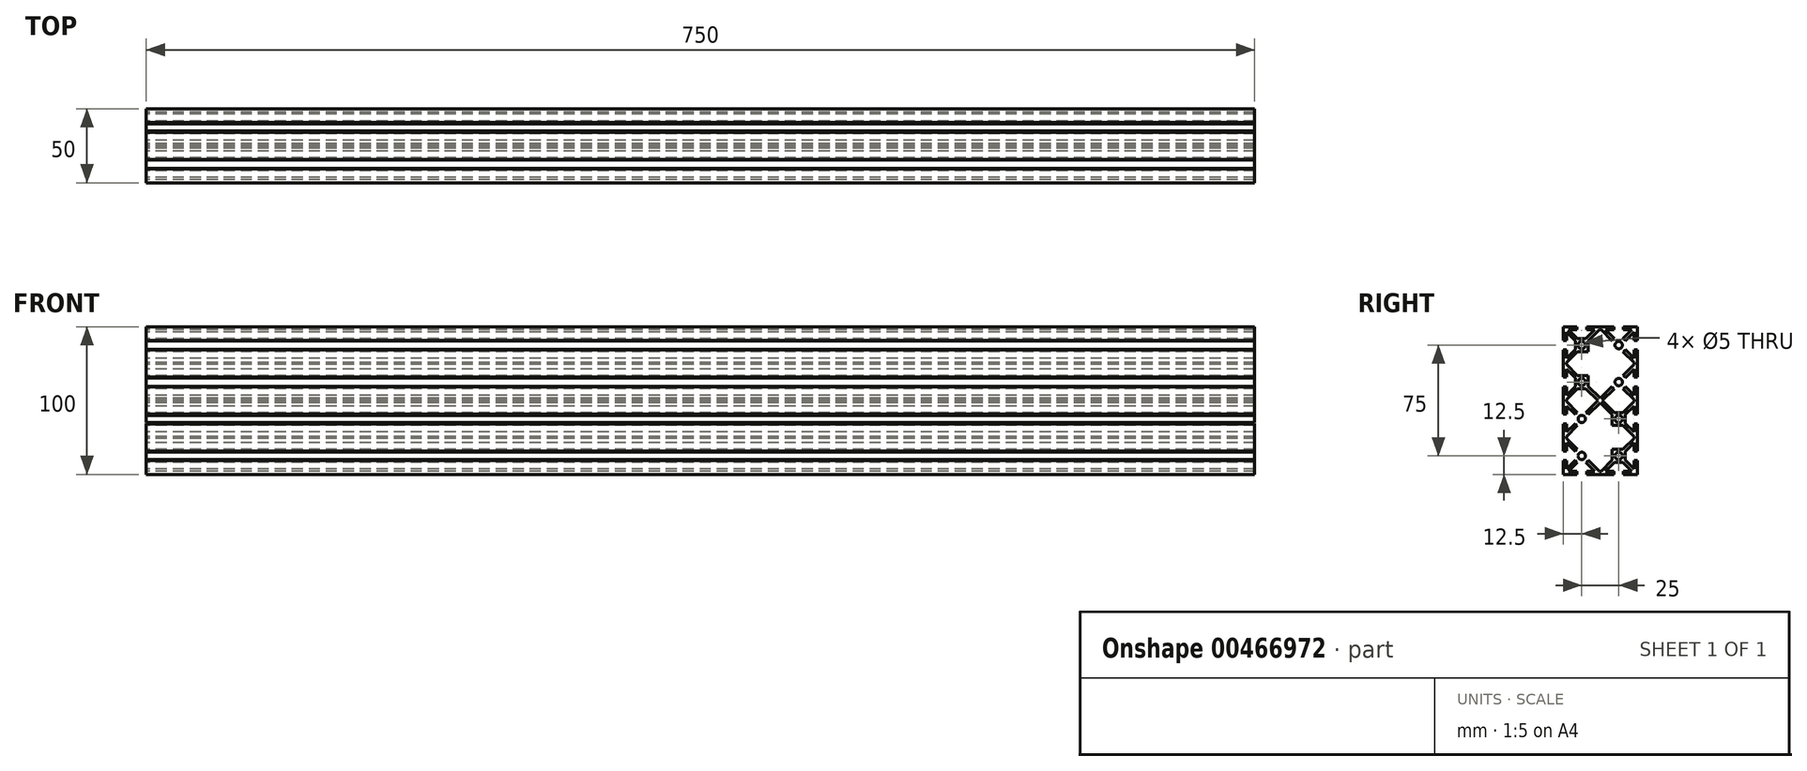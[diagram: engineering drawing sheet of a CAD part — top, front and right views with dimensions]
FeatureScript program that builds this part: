
annotation { "Feature Type Name" : "Feature", "Feature Type Description" : "" }
export const myFeature = defineFeature(function(context is Context, id is Id, definition is map)
    precondition{}
    {
        {
            var Q0;
            Q0=qCreatedBy(makeId("Right.planeOp"),FACE);
            var sketch = newSketch(context, id + "F0", { "sketchPlane" : qUnion([Q0])});
            skLineSegment(sketch, "E0", {"start": v(0, 0) * mm, "end": v(-22.87, 0) * mm, "construction": true});
            skLineSegment(sketch, "E1", {"start": v(0, 0) * mm, "end": v(0, 47.87) * mm, "construction": true});
            skCircle(sketch, "E2", {"center": v(-12.5, 37.5) * mm, "radius": 2.5 * mm});
            skCircle(sketch, "E3", {"center": v(-12.5, 12.5) * mm, "radius": 2.5 * mm});
            skLineSegment(sketch, "E4.bottom", {"start": v(-8.12, 41.88) * mm, "end": v(-16.88, 41.88) * mm});
            skLineSegment(sketch, "E4.top", {"start": v(-8.12, 33.12) * mm, "end": v(-16.88, 33.12) * mm});
            skLineSegment(sketch, "E4.left", {"start": v(-8.12, 41.88) * mm, "end": v(-8.12, 33.12) * mm});
            skLineSegment(sketch, "E4.right", {"start": v(-16.88, 41.88) * mm, "end": v(-16.88, 33.12) * mm});
            skLineSegment(sketch, "E5.bottom", {"start": v(-8.12, 16.88) * mm, "end": v(-16.88, 16.88) * mm});
            skLineSegment(sketch, "E5.top", {"start": v(-8.12, 8.12) * mm, "end": v(-16.88, 8.12) * mm});
            skLineSegment(sketch, "E5.left", {"start": v(-8.12, 16.88) * mm, "end": v(-8.12, 8.12) * mm});
            skLineSegment(sketch, "E5.right", {"start": v(-16.88, 16.88) * mm, "end": v(-16.88, 8.12) * mm});
            skLineSegment(sketch, "E6", {"start": v(0, 50) * mm, "end": v(-9.25, 50) * mm});
            skLineSegment(sketch, "E7", {"start": v(-9.25, 50) * mm, "end": v(-9.25, 47.87) * mm});
            skLineSegment(sketch, "E8", {"start": v(-9.25, 47.87) * mm, "end": v(-3.64, 47.87) * mm});
            skLineSegment(sketch, "E9", {"start": v(-3.64, 47.87) * mm, "end": v(-9.63, 41.88) * mm});
            skLineSegment(sketch, "E10", {"start": v(-15.37, 41.88) * mm, "end": v(-21.36, 47.87) * mm});
            skLineSegment(sketch, "E11", {"start": v(-21.36, 47.87) * mm, "end": v(-15.75, 47.87) * mm});
            skLineSegment(sketch, "E12", {"start": v(-15.75, 47.87) * mm, "end": v(-15.75, 50) * mm});
            skLineSegment(sketch, "E13", {"start": v(-15.75, 50) * mm, "end": v(-25, 50) * mm});
            skLineSegment(sketch, "E14", {"start": v(-25, 50) * mm, "end": v(-25, 40.75) * mm});
            skLineSegment(sketch, "E15", {"start": v(-25, 40.75) * mm, "end": v(-22.87, 40.75) * mm});
            skLineSegment(sketch, "E16", {"start": v(-22.87, 40.75) * mm, "end": v(-22.87, 46.36) * mm});
            skLineSegment(sketch, "E17", {"start": v(-22.87, 46.36) * mm, "end": v(-16.88, 40.37) * mm});
            skLineSegment(sketch, "E18", {"start": v(-16.88, 34.63) * mm, "end": v(-22.87, 28.64) * mm});
            skLineSegment(sketch, "E19", {"start": v(-22.87, 28.64) * mm, "end": v(-22.87, 34.25) * mm});
            skLineSegment(sketch, "E20", {"start": v(-22.87, 34.25) * mm, "end": v(-25, 34.25) * mm});
            skLineSegment(sketch, "E21", {"start": v(-25, 34.25) * mm, "end": v(-25, 15.75) * mm});
            skLineSegment(sketch, "E22", {"start": v(-25, 15.75) * mm, "end": v(-22.87, 15.75) * mm});
            skLineSegment(sketch, "E23", {"start": v(-22.87, 15.75) * mm, "end": v(-22.87, 21.36) * mm});
            skLineSegment(sketch, "E24", {"start": v(-22.87, 21.36) * mm, "end": v(-16.88, 15.37) * mm});
            skLineSegment(sketch, "E25", {"start": v(-16.88, 9.63) * mm, "end": v(-22.87, 3.64) * mm});
            skLineSegment(sketch, "E26", {"start": v(-22.87, 3.64) * mm, "end": v(-22.87, 9.25) * mm});
            skLineSegment(sketch, "E27", {"start": v(-22.87, 9.25) * mm, "end": v(-25, 9.25) * mm});
            skLineSegment(sketch, "E28", {"start": v(-25, 9.25) * mm, "end": v(-25, 0) * mm});
            skLineSegment(sketch, "E29", {"start": v(-23.93, 9.25) * mm, "end": v(-23.94, 15.75) * mm, "construction": true});
            skLineSegment(sketch, "E30", {"start": v(-23.94, 34.25) * mm, "end": v(-23.94, 40.75) * mm, "construction": true});
            skLineSegment(sketch, "E31", {"start": v(-9.25, 48.94) * mm, "end": v(-15.75, 48.94) * mm, "construction": true});
            skLineSegment(sketch, "E32", {"start": v(-21.36, 47.87) * mm, "end": v(-22.87, 46.36) * mm, "construction": true});
            skLineSegment(sketch, "E33", {"start": v(-12.5, 48.94) * mm, "end": v(-12.5, 37.5) * mm, "construction": true});
            skLineSegment(sketch, "E34", {"start": v(-23.94, 37.5) * mm, "end": v(-12.5, 37.5) * mm, "construction": true});
            skLineSegment(sketch, "E35", {"start": v(-23.93, 12.5) * mm, "end": v(-12.5, 12.5) * mm, "construction": true});
            skLineSegment(sketch, "E36", {"start": v(-22.87, 0) * mm, "end": v(-22.87, 0.62) * mm});
            skLineSegment(sketch, "E37", {"start": v(-22.87, 0.62) * mm, "end": v(-15.37, 8.12) * mm});
            skLineSegment(sketch, "E38", {"start": v(-15.37, 16.88) * mm, "end": v(-22.87, 24.38) * mm});
            skLineSegment(sketch, "E39", {"start": v(-22.87, 24.38) * mm, "end": v(-22.87, 25.62) * mm});
            skLineSegment(sketch, "E40", {"start": v(-22.87, 25.62) * mm, "end": v(-15.37, 33.12) * mm});
            skLineSegment(sketch, "E41", {"start": v(-22.87, 21.36) * mm, "end": v(-21.36, 22.87) * mm, "construction": true});
            skLineSegment(sketch, "E42", {"start": v(-21.36, 27.13) * mm, "end": v(-22.87, 28.64) * mm, "construction": true});
            skLineSegment(sketch, "E43", {"start": v(-22.87, 3.64) * mm, "end": v(-21.36, 2.13) * mm, "construction": true});
            skLineSegment(sketch, "E44", {"start": v(-22.12, 2.88) * mm, "end": v(-16.88, 8.12) * mm, "construction": true});
            skLineSegment(sketch, "E45", {"start": v(-22.12, 22.12) * mm, "end": v(-16.88, 16.88) * mm, "construction": true});
            skLineSegment(sketch, "E46", {"start": v(-22.12, 27.88) * mm, "end": v(-16.88, 33.12) * mm, "construction": true});
            skLineSegment(sketch, "E47", {"start": v(-22.12, 47.12) * mm, "end": v(-16.88, 41.88) * mm, "construction": true});
            skLineSegment(sketch, "E48", {"start": v(-8.12, 40.37) * mm, "end": v(-0.62, 47.87) * mm});
            skLineSegment(sketch, "E49", {"start": v(-0.62, 47.87) * mm, "end": v(0, 47.87) * mm});
            skLineSegment(sketch, "E50", {"start": v(-8.12, 9.63) * mm, "end": v(0, 1.5) * mm});
            skLineSegment(sketch, "E51", {"start": v(-1.5, 0) * mm, "end": v(-9.63, 8.12) * mm});
            skLineSegment(sketch, "E52.MirrorCS", {"start": v(0.62, 47.87) * mm, "end": v(0, 47.87) * mm});
            skLineSegment(sketch, "E53.MirrorCS", {"start": v(22.87, 24.38) * mm, "end": v(22.87, 25.62) * mm});
            skLineSegment(sketch, "E54.MirrorCS", {"start": v(22.87, 0) * mm, "end": v(22.87, 0.62) * mm});
            skLineSegment(sketch, "E55.MirrorCS", {"start": v(22.87, 21.36) * mm, "end": v(21.36, 22.87) * mm, "construction": true});
            skLineSegment(sketch, "E56.MirrorCS", {"start": v(21.36, 47.87) * mm, "end": v(22.87, 46.36) * mm, "construction": true});
            skLineSegment(sketch, "E57.MirrorCS", {"start": v(9.25, 50) * mm, "end": v(9.25, 47.87) * mm});
            skLineSegment(sketch, "E58.MirrorCS", {"start": v(25, 40.75) * mm, "end": v(22.87, 40.75) * mm});
            skLineSegment(sketch, "E59.MirrorCS", {"start": v(25, 15.75) * mm, "end": v(22.87, 15.75) * mm});
            skLineSegment(sketch, "E60.MirrorCS", {"start": v(15.75, 47.87) * mm, "end": v(15.75, 50) * mm});
            skLineSegment(sketch, "E61.MirrorCS", {"start": v(22.87, 9.25) * mm, "end": v(25, 9.25) * mm});
            skLineSegment(sketch, "E62.MirrorCS", {"start": v(22.87, 34.25) * mm, "end": v(25, 34.25) * mm});
            skLineSegment(sketch, "E63.MirrorCS", {"start": v(21.36, 27.13) * mm, "end": v(22.87, 28.64) * mm, "construction": true});
            skLineSegment(sketch, "E64.MirrorCS", {"start": v(22.87, 3.64) * mm, "end": v(21.36, 2.13) * mm, "construction": true});
            skLineSegment(sketch, "E65.MirrorCS", {"start": v(22.87, 40.75) * mm, "end": v(22.87, 46.36) * mm});
            skLineSegment(sketch, "E66.MirrorCS", {"start": v(8.12, 40.37) * mm, "end": v(0.62, 47.87) * mm});
            skLineSegment(sketch, "E67.MirrorCS", {"start": v(16.88, 9.63) * mm, "end": v(22.87, 3.64) * mm});
            skLineSegment(sketch, "E68.MirrorCS", {"start": v(9.25, 47.87) * mm, "end": v(3.64, 47.87) * mm});
            skLineSegment(sketch, "E69.MirrorCS", {"start": v(3.64, 47.87) * mm, "end": v(9.63, 41.88) * mm});
            skLineSegment(sketch, "E70.MirrorCS", {"start": v(0, 0) * mm, "end": v(22.87, 0) * mm, "construction": true});
            skCircle(sketch, "E71.MirrorC", {"center": v(12.5, 37.5) * mm, "radius": 2.5 * mm});
            skCircle(sketch, "E72.MirrorC", {"center": v(12.5, 12.5) * mm, "radius": 2.5 * mm});
            skLineSegment(sketch, "E73.MirrorCS", {"start": v(8.12, 41.88) * mm, "end": v(16.88, 41.88) * mm});
            skLineSegment(sketch, "E74.MirrorCS", {"start": v(8.12, 33.12) * mm, "end": v(16.88, 33.12) * mm});
            skLineSegment(sketch, "E75.MirrorCS", {"start": v(8.12, 41.88) * mm, "end": v(8.12, 33.12) * mm});
            skLineSegment(sketch, "E76.MirrorCS", {"start": v(16.88, 41.88) * mm, "end": v(16.88, 33.12) * mm});
            skLineSegment(sketch, "E77.MirrorCS", {"start": v(8.12, 16.88) * mm, "end": v(16.88, 16.88) * mm});
            skLineSegment(sketch, "E78.MirrorCS", {"start": v(8.12, 8.12) * mm, "end": v(16.88, 8.12) * mm});
            skLineSegment(sketch, "E79.MirrorCS", {"start": v(22.87, 21.36) * mm, "end": v(16.88, 15.37) * mm});
            skLineSegment(sketch, "E80.MirrorCS", {"start": v(9.25, 48.94) * mm, "end": v(15.75, 48.94) * mm, "construction": true});
            skLineSegment(sketch, "E81.MirrorCS", {"start": v(22.12, 47.12) * mm, "end": v(16.88, 41.88) * mm, "construction": true});
            skLineSegment(sketch, "E82.MirrorCS", {"start": v(22.87, 25.62) * mm, "end": v(15.37, 33.12) * mm});
            skLineSegment(sketch, "E83.MirrorCS", {"start": v(15.37, 16.88) * mm, "end": v(22.87, 24.38) * mm});
            skLineSegment(sketch, "E84.MirrorCS", {"start": v(23.94, 34.25) * mm, "end": v(23.94, 40.75) * mm, "construction": true});
            skLineSegment(sketch, "E85.MirrorCS", {"start": v(8.12, 16.88) * mm, "end": v(8.12, 8.12) * mm});
            skLineSegment(sketch, "E86.MirrorCS", {"start": v(22.87, 15.75) * mm, "end": v(22.87, 21.36) * mm});
            skLineSegment(sketch, "E87.MirrorCS", {"start": v(16.88, 34.63) * mm, "end": v(22.87, 28.64) * mm});
            skLineSegment(sketch, "E88.MirrorCS", {"start": v(22.87, 46.36) * mm, "end": v(16.88, 40.37) * mm});
            skLineSegment(sketch, "E89.MirrorCS", {"start": v(12.5, 48.94) * mm, "end": v(12.5, 37.5) * mm, "construction": true});
            skLineSegment(sketch, "E90.MirrorCS", {"start": v(21.36, 47.87) * mm, "end": v(15.75, 47.87) * mm});
            skLineSegment(sketch, "E91.MirrorCS", {"start": v(22.12, 27.88) * mm, "end": v(16.88, 33.12) * mm, "construction": true});
            skLineSegment(sketch, "E92.MirrorCS", {"start": v(23.94, 37.5) * mm, "end": v(12.5, 37.5) * mm, "construction": true});
            skLineSegment(sketch, "E93.MirrorCS", {"start": v(8.12, 9.63) * mm, "end": v(0, 1.5) * mm});
            skLineSegment(sketch, "E94.MirrorCS", {"start": v(22.87, 28.64) * mm, "end": v(22.87, 34.25) * mm});
            skLineSegment(sketch, "E95.MirrorCS", {"start": v(15.37, 41.88) * mm, "end": v(21.36, 47.87) * mm});
            skLineSegment(sketch, "E96.MirrorCS", {"start": v(22.87, 3.64) * mm, "end": v(22.87, 9.25) * mm});
            skLineSegment(sketch, "E97.MirrorCS", {"start": v(25, 9.25) * mm, "end": v(25, 0) * mm});
            skLineSegment(sketch, "E98.MirrorCS", {"start": v(23.93, 9.25) * mm, "end": v(23.94, 15.75) * mm, "construction": true});
            skLineSegment(sketch, "E99.MirrorCS", {"start": v(22.12, 22.12) * mm, "end": v(16.88, 16.88) * mm, "construction": true});
            skLineSegment(sketch, "E100.MirrorCS", {"start": v(22.12, 2.88) * mm, "end": v(16.88, 8.12) * mm, "construction": true});
            skLineSegment(sketch, "E101.MirrorCS", {"start": v(23.93, 12.5) * mm, "end": v(12.5, 12.5) * mm, "construction": true});
            skLineSegment(sketch, "E102.MirrorCS", {"start": v(25, 50) * mm, "end": v(25, 40.75) * mm});
            skLineSegment(sketch, "E103.MirrorCS", {"start": v(15.75, 50) * mm, "end": v(25, 50) * mm});
            skLineSegment(sketch, "E104.MirrorCS", {"start": v(16.88, 16.88) * mm, "end": v(16.88, 8.12) * mm});
            skLineSegment(sketch, "E105.MirrorCS", {"start": v(22.87, 0.62) * mm, "end": v(15.37, 8.12) * mm});
            skLineSegment(sketch, "E106.MirrorCS", {"start": v(0, 50) * mm, "end": v(9.25, 50) * mm});
            skLineSegment(sketch, "E107.MirrorCS", {"start": v(1.5, 0) * mm, "end": v(9.63, 8.12) * mm});
            skLineSegment(sketch, "E108.MirrorCS", {"start": v(25, 34.25) * mm, "end": v(25, 15.75) * mm});
            skLineSegment(sketch, "E109.MirrorCS", {"start": v(-0.62, -47.87) * mm, "end": v(0, -47.87) * mm});
            skLineSegment(sketch, "E110.MirrorCS", {"start": v(21.36, -47.87) * mm, "end": v(22.87, -46.36) * mm, "construction": true});
            skLineSegment(sketch, "E111.MirrorCS", {"start": v(-21.36, -47.87) * mm, "end": v(-22.87, -46.36) * mm, "construction": true});
            skLineSegment(sketch, "E112.MirrorCS", {"start": v(0.62, -47.87) * mm, "end": v(0, -47.87) * mm});
            skLineSegment(sketch, "E113.MirrorCS", {"start": v(25, -40.75) * mm, "end": v(22.87, -40.75) * mm});
            skLineSegment(sketch, "E114.MirrorCS", {"start": v(-22.87, -24.38) * mm, "end": v(-22.87, -25.62) * mm});
            skLineSegment(sketch, "E115.MirrorCS", {"start": v(22.87, -34.25) * mm, "end": v(25, -34.25) * mm});
            skLineSegment(sketch, "E116.MirrorCS", {"start": v(22.87, -24.38) * mm, "end": v(22.87, -25.62) * mm});
            skLineSegment(sketch, "E117.MirrorCS", {"start": v(22.87, 0) * mm, "end": v(22.87, -0.62) * mm});
            skLineSegment(sketch, "E118.MirrorCS", {"start": v(-25, -15.75) * mm, "end": v(-22.87, -15.75) * mm});
            skLineSegment(sketch, "E119.MirrorCS", {"start": v(-25, -40.75) * mm, "end": v(-22.87, -40.75) * mm});
            skLineSegment(sketch, "E120.MirrorCS", {"start": v(25, -15.75) * mm, "end": v(22.87, -15.75) * mm});
            skLineSegment(sketch, "E121.MirrorCS", {"start": v(22.87, -9.25) * mm, "end": v(25, -9.25) * mm});
            skLineSegment(sketch, "E122.MirrorCS", {"start": v(-9.25, -50) * mm, "end": v(-9.25, -47.87) * mm});
            skLineSegment(sketch, "E123.MirrorCS", {"start": v(-22.87, 0) * mm, "end": v(-22.87, -0.62) * mm});
            skLineSegment(sketch, "E124.MirrorCS", {"start": v(9.25, -50) * mm, "end": v(9.25, -47.87) * mm});
            skLineSegment(sketch, "E125.MirrorCS", {"start": v(-15.75, -47.87) * mm, "end": v(-15.75, -50) * mm});
            skLineSegment(sketch, "E126.MirrorCS", {"start": v(-22.87, -34.25) * mm, "end": v(-25, -34.25) * mm});
            skLineSegment(sketch, "E127.MirrorCS", {"start": v(-22.87, -9.25) * mm, "end": v(-25, -9.25) * mm});
            skLineSegment(sketch, "E128.MirrorCS", {"start": v(15.75, -47.87) * mm, "end": v(15.75, -50) * mm});
            skLineSegment(sketch, "E129.MirrorCS", {"start": v(-21.36, -27.13) * mm, "end": v(-22.87, -28.64) * mm, "construction": true});
            skLineSegment(sketch, "E130.MirrorCS", {"start": v(22.87, -21.36) * mm, "end": v(21.36, -22.87) * mm, "construction": true});
            skLineSegment(sketch, "E131.MirrorCS", {"start": v(21.36, -27.13) * mm, "end": v(22.87, -28.64) * mm, "construction": true});
            skLineSegment(sketch, "E132.MirrorCS", {"start": v(-22.87, -3.64) * mm, "end": v(-21.36, -2.13) * mm, "construction": true});
            skLineSegment(sketch, "E133.MirrorCS", {"start": v(-22.87, -21.36) * mm, "end": v(-21.36, -22.87) * mm, "construction": true});
            skLineSegment(sketch, "E134.MirrorCS", {"start": v(22.87, -3.64) * mm, "end": v(21.36, -2.13) * mm, "construction": true});
            skLineSegment(sketch, "E135.MirrorCS", {"start": v(23.94, -37.5) * mm, "end": v(12.5, -37.5) * mm, "construction": true});
            skLineSegment(sketch, "E136.MirrorCS", {"start": v(22.87, -28.64) * mm, "end": v(22.87, -34.25) * mm});
            skLineSegment(sketch, "E137.MirrorCS", {"start": v(16.88, -34.63) * mm, "end": v(22.87, -28.64) * mm});
            skLineSegment(sketch, "E138.MirrorCS", {"start": v(8.12, -33.12) * mm, "end": v(16.88, -33.12) * mm});
            skLineSegment(sketch, "E139.MirrorCS", {"start": v(-22.87, -3.64) * mm, "end": v(-22.87, -9.25) * mm});
            skLineSegment(sketch, "E140.MirrorCS", {"start": v(15.75, -50) * mm, "end": v(25, -50) * mm});
            skLineSegment(sketch, "E141.MirrorCS", {"start": v(-15.37, -41.88) * mm, "end": v(-21.36, -47.87) * mm});
            skPoint(sketch, "E142.MirrorP", {"position": v(-12.5, -37.5) * mm});
            skLineSegment(sketch, "E143.MirrorCS", {"start": v(22.87, -40.75) * mm, "end": v(22.87, -46.36) * mm});
            skLineSegment(sketch, "E144.MirrorCS", {"start": v(22.12, -47.12) * mm, "end": v(16.88, -41.88) * mm, "construction": true});
            skLineSegment(sketch, "E145.MirrorCS", {"start": v(-22.87, -15.75) * mm, "end": v(-22.87, -21.36) * mm});
            skLineSegment(sketch, "E146.MirrorCS", {"start": v(-23.94, -34.25) * mm, "end": v(-23.94, -40.75) * mm, "construction": true});
            skLineSegment(sketch, "E147.MirrorCS", {"start": v(-22.12, -27.88) * mm, "end": v(-16.88, -33.12) * mm, "construction": true});
            skLineSegment(sketch, "E148.MirrorCS", {"start": v(25, -9.25) * mm, "end": v(25, 0) * mm});
            skLineSegment(sketch, "E149.MirrorCS", {"start": v(-22.87, -46.36) * mm, "end": v(-16.88, -40.37) * mm});
            skLineSegment(sketch, "E150.MirrorCS", {"start": v(-8.12, -9.63) * mm, "end": v(0, -1.5) * mm});
            skLineSegment(sketch, "E151.MirrorCS", {"start": v(-12.5, -48.94) * mm, "end": v(-12.5, -37.5) * mm, "construction": true});
            skLineSegment(sketch, "E152.MirrorCS", {"start": v(-16.88, -34.63) * mm, "end": v(-22.87, -28.64) * mm});
            skLineSegment(sketch, "E153.MirrorCS", {"start": v(-23.94, -37.5) * mm, "end": v(-12.5, -37.5) * mm, "construction": true});
            skLineSegment(sketch, "E154.MirrorCS", {"start": v(21.36, -47.87) * mm, "end": v(15.75, -47.87) * mm});
            skLineSegment(sketch, "E155.MirrorCS", {"start": v(23.93, -9.25) * mm, "end": v(23.94, -15.75) * mm, "construction": true});
            skLineSegment(sketch, "E156.MirrorCS", {"start": v(0, -50) * mm, "end": v(9.25, -50) * mm});
            skLineSegment(sketch, "E157.MirrorCS", {"start": v(8.12, -8.12) * mm, "end": v(16.88, -8.12) * mm});
            skCircle(sketch, "E158.MirrorC", {"center": v(12.5, -37.5) * mm, "radius": 2.5 * mm});
            skLineSegment(sketch, "E159.MirrorCS", {"start": v(22.87, -25.62) * mm, "end": v(15.37, -33.12) * mm});
            skLineSegment(sketch, "E160.MirrorCS", {"start": v(8.12, -40.37) * mm, "end": v(0.62, -47.87) * mm});
            skLineSegment(sketch, "E161.MirrorCS", {"start": v(0, -50) * mm, "end": v(-9.25, -50) * mm});
            skLineSegment(sketch, "E162.MirrorCS", {"start": v(-25, -50) * mm, "end": v(-25, -40.75) * mm});
            skLineSegment(sketch, "E163.MirrorCS", {"start": v(3.64, -47.87) * mm, "end": v(9.63, -41.88) * mm});
            skLineSegment(sketch, "E164.MirrorCS", {"start": v(-16.88, -16.88) * mm, "end": v(-16.88, -8.12) * mm});
            skPoint(sketch, "E165.MirrorP", {"position": v(-12.5, -12.5) * mm});
            skLineSegment(sketch, "E166.MirrorCS", {"start": v(8.12, -16.88) * mm, "end": v(8.12, -8.12) * mm});
            skLineSegment(sketch, "E167.MirrorCS", {"start": v(23.93, -12.5) * mm, "end": v(12.5, -12.5) * mm, "construction": true});
            skLineSegment(sketch, "E168.MirrorCS", {"start": v(-25, -34.25) * mm, "end": v(-25, -15.75) * mm});
            skLineSegment(sketch, "E169.MirrorCS", {"start": v(-22.87, -0.62) * mm, "end": v(-15.37, -8.12) * mm});
            skPoint(sketch, "E170.MirrorP", {"position": v(12.5, -12.5) * mm});
            skLineSegment(sketch, "E171.MirrorCS", {"start": v(-8.12, -16.88) * mm, "end": v(-8.12, -8.12) * mm});
            skLineSegment(sketch, "E172.MirrorCS", {"start": v(-8.12, -8.12) * mm, "end": v(-16.88, -8.12) * mm});
            skLineSegment(sketch, "E173.MirrorCS", {"start": v(-15.37, -16.88) * mm, "end": v(-22.87, -24.38) * mm});
            skLineSegment(sketch, "E174.MirrorCS", {"start": v(25, -50) * mm, "end": v(25, -40.75) * mm});
            skLineSegment(sketch, "E175.MirrorCS", {"start": v(22.87, -15.75) * mm, "end": v(22.87, -21.36) * mm});
            skLineSegment(sketch, "E176.MirrorCS", {"start": v(-8.12, -16.88) * mm, "end": v(-16.88, -16.88) * mm});
            skCircle(sketch, "E177.MirrorC", {"center": v(12.5, -12.5) * mm, "radius": 2.5 * mm});
            skLineSegment(sketch, "E178.MirrorCS", {"start": v(22.87, -21.36) * mm, "end": v(16.88, -15.37) * mm});
            skLineSegment(sketch, "E179.MirrorCS", {"start": v(-16.88, -41.88) * mm, "end": v(-16.88, -33.12) * mm});
            skLineSegment(sketch, "E180.MirrorCS", {"start": v(-21.36, -47.87) * mm, "end": v(-15.75, -47.87) * mm});
            skLineSegment(sketch, "E181.MirrorCS", {"start": v(-8.12, -41.88) * mm, "end": v(-8.12, -33.12) * mm});
            skLineSegment(sketch, "E182.MirrorCS", {"start": v(8.12, -41.88) * mm, "end": v(8.12, -33.12) * mm});
            skLineSegment(sketch, "E183.MirrorCS", {"start": v(-8.12, -33.12) * mm, "end": v(-16.88, -33.12) * mm});
            skLineSegment(sketch, "E184.MirrorCS", {"start": v(-8.12, -41.88) * mm, "end": v(-16.88, -41.88) * mm});
            skLineSegment(sketch, "E185.MirrorCS", {"start": v(-22.12, -22.12) * mm, "end": v(-16.88, -16.88) * mm, "construction": true});
            skLineSegment(sketch, "E186.MirrorCS", {"start": v(25, -34.25) * mm, "end": v(25, -15.75) * mm});
            skLineSegment(sketch, "E187.MirrorCS", {"start": v(-25, -9.25) * mm, "end": v(-25, 0) * mm});
            skLineSegment(sketch, "E188.MirrorCS", {"start": v(-1.5, 0) * mm, "end": v(-9.63, -8.12) * mm});
            skLineSegment(sketch, "E189.MirrorCS", {"start": v(12.5, -48.94) * mm, "end": v(12.5, -37.5) * mm, "construction": true});
            skLineSegment(sketch, "E190.MirrorCS", {"start": v(-22.12, -47.12) * mm, "end": v(-16.88, -41.88) * mm, "construction": true});
            skLineSegment(sketch, "E191.MirrorCS", {"start": v(-22.87, -25.62) * mm, "end": v(-15.37, -33.12) * mm});
            skCircle(sketch, "E192.MirrorC", {"center": v(-12.5, -12.5) * mm, "radius": 2.5 * mm});
            skLineSegment(sketch, "E193.MirrorCS", {"start": v(22.87, -3.64) * mm, "end": v(22.87, -9.25) * mm});
            skLineSegment(sketch, "E194.MirrorCS", {"start": v(-9.25, -47.87) * mm, "end": v(-3.64, -47.87) * mm});
            skLineSegment(sketch, "E195.MirrorCS", {"start": v(-23.93, -9.25) * mm, "end": v(-23.94, -15.75) * mm, "construction": true});
            skLineSegment(sketch, "E196.MirrorCS", {"start": v(-3.64, -47.87) * mm, "end": v(-9.63, -41.88) * mm});
            skLineSegment(sketch, "E197.MirrorCS", {"start": v(-23.93, -12.5) * mm, "end": v(-12.5, -12.5) * mm, "construction": true});
            skLineSegment(sketch, "E198.MirrorCS", {"start": v(22.87, -0.62) * mm, "end": v(15.37, -8.12) * mm});
            skLineSegment(sketch, "E199.MirrorCS", {"start": v(15.37, -16.88) * mm, "end": v(22.87, -24.38) * mm});
            skLineSegment(sketch, "E200.MirrorCS", {"start": v(8.12, -9.63) * mm, "end": v(0, -1.5) * mm});
            skCircle(sketch, "E201.MirrorC", {"center": v(-12.5, -37.5) * mm, "radius": 2.5 * mm});
            skLineSegment(sketch, "E202.MirrorCS", {"start": v(16.88, -41.88) * mm, "end": v(16.88, -33.12) * mm});
            skLineSegment(sketch, "E203.MirrorCS", {"start": v(16.88, -9.63) * mm, "end": v(22.87, -3.64) * mm});
            skLineSegment(sketch, "E204.MirrorCS", {"start": v(8.12, -16.88) * mm, "end": v(16.88, -16.88) * mm});
            skLineSegment(sketch, "E205.MirrorCS", {"start": v(-16.88, -9.63) * mm, "end": v(-22.87, -3.64) * mm});
            skLineSegment(sketch, "E206.MirrorCS", {"start": v(-22.87, -21.36) * mm, "end": v(-16.88, -15.37) * mm});
            skLineSegment(sketch, "E207.MirrorCS", {"start": v(1.5, 0) * mm, "end": v(9.63, -8.12) * mm});
            skLineSegment(sketch, "E208.MirrorCS", {"start": v(22.12, -27.88) * mm, "end": v(16.88, -33.12) * mm, "construction": true});
            skLineSegment(sketch, "E209.MirrorCS", {"start": v(22.12, -22.12) * mm, "end": v(16.88, -16.88) * mm, "construction": true});
            skLineSegment(sketch, "E210.MirrorCS", {"start": v(-9.25, -48.94) * mm, "end": v(-15.75, -48.94) * mm, "construction": true});
            skLineSegment(sketch, "E211.MirrorCS", {"start": v(22.87, -46.36) * mm, "end": v(16.88, -40.37) * mm});
            skLineSegment(sketch, "E212.MirrorCS", {"start": v(-8.12, -40.37) * mm, "end": v(-0.62, -47.87) * mm});
            skLineSegment(sketch, "E213.MirrorCS", {"start": v(23.94, -34.25) * mm, "end": v(23.94, -40.75) * mm, "construction": true});
            skLineSegment(sketch, "E214.MirrorCS", {"start": v(-22.12, -2.88) * mm, "end": v(-16.88, -8.12) * mm, "construction": true});
            skLineSegment(sketch, "E215.MirrorCS", {"start": v(-15.75, -50) * mm, "end": v(-25, -50) * mm});
            skLineSegment(sketch, "E216.MirrorCS", {"start": v(0, 0) * mm, "end": v(0, -47.87) * mm, "construction": true});
            skLineSegment(sketch, "E217.MirrorCS", {"start": v(16.88, -16.88) * mm, "end": v(16.88, -8.12) * mm});
            skLineSegment(sketch, "E218.MirrorCS", {"start": v(9.25, -48.94) * mm, "end": v(15.75, -48.94) * mm, "construction": true});
            skLineSegment(sketch, "E219.MirrorCS", {"start": v(22.12, -2.88) * mm, "end": v(16.88, -8.12) * mm, "construction": true});
            skLineSegment(sketch, "E220.MirrorCS", {"start": v(8.12, -41.88) * mm, "end": v(16.88, -41.88) * mm});
            skLineSegment(sketch, "E221.MirrorCS", {"start": v(-22.87, -28.64) * mm, "end": v(-22.87, -34.25) * mm});
            skLineSegment(sketch, "E222.MirrorCS", {"start": v(9.25, -47.87) * mm, "end": v(3.64, -47.87) * mm});
            skLineSegment(sketch, "E223.MirrorCS", {"start": v(15.37, -41.88) * mm, "end": v(21.36, -47.87) * mm});
            skLineSegment(sketch, "E224.MirrorCS", {"start": v(-22.87, -40.75) * mm, "end": v(-22.87, -46.36) * mm});
            skSolve(sketch);
        }
        {
            var Q0;
            {var subQ4=sQuery(id+"F0.wireOp",EDGE,"E18");Q0=makeQuery(id+"F0.imprint","IMPRINT",FACE,{"disambiguationData":[TD([[makeQuery(id+"F0.imprint","IMPRINT",EDGE,{"derivedFrom":subQ4}),1.0]])]});}
            var Q1;
            Q1=makeQuery(id+"F0.imprint","IMPRINT",FACE,{"disambiguationData":[TD([[makeQuery(id+"F0.imprint","IMPRINT",EDGE,{"derivedFrom":sQuery(id+"F0.wireOp",EDGE,"E2")}),-1.0]])]});
            var Q2;
            {var subQ0=sQuery(id+"F0.wireOp",EDGE,"E10");Q2=makeQuery(id+"F0.imprint","IMPRINT",FACE,{"disambiguationData":[TD([[makeQuery(id+"F0.imprint","IMPRINT",EDGE,{"derivedFrom":subQ0}),1.0]])]});}
            var Q3;
            Q3=makeQuery(id+"F0.imprint","IMPRINT",FACE,{"disambiguationData":[TD([[makeQuery(id+"F0.imprint","IMPRINT",EDGE,{"derivedFrom":sQuery(id+"F0.wireOp",EDGE,"E6")}),1.0]])]});
            var Q4;
            Q4=makeQuery(id+"F0.imprint","IMPRINT",FACE,{"disambiguationData":[TD([[makeQuery(id+"F0.imprint","IMPRINT",EDGE,{"derivedFrom":sQuery(id+"F0.wireOp",EDGE,"E71.MirrorC")}),1.0]])]});
            var Q5;
            Q5=makeQuery(id+"F0.imprint","IMPRINT",FACE,{"disambiguationData":[TD([[makeQuery(id+"F0.imprint","IMPRINT",EDGE,{"derivedFrom":sQuery(id+"F0.wireOp",EDGE,"E109.MirrorCS")}),-1.0]])]});
            var Q6;
            Q6=makeQuery(id+"F0.imprint","IMPRINT",FACE,{"disambiguationData":[TD([[makeQuery(id+"F0.imprint","IMPRINT",EDGE,{"derivedFrom":sQuery(id+"F0.wireOp",EDGE,"E177.MirrorC")}),-1.0]])]});
            var Q7;
            Q7=makeQuery(id+"F0.imprint","IMPRINT",FACE,{"disambiguationData":[TD([[makeQuery(id+"F0.imprint","IMPRINT",EDGE,{"derivedFrom":sQuery(id+"F0.wireOp",EDGE,"E115.MirrorCS")}),1.0]])]});
            var Q8;
            Q8=makeQuery(id+"F0.imprint","IMPRINT",FACE,{"disambiguationData":[TD([[makeQuery(id+"F0.imprint","IMPRINT",EDGE,{"derivedFrom":sQuery(id+"F0.wireOp",EDGE,"E3")}),-1.0]])]});
            var Q9;
            Q9=makeQuery(id+"F0.imprint","IMPRINT",FACE,{"disambiguationData":[TD([[makeQuery(id+"F0.imprint","IMPRINT",EDGE,{"derivedFrom":sQuery(id+"F0.wireOp",EDGE,"E72.MirrorC")}),1.0]])]});
            var Q10;
            Q10=makeQuery(id+"F0.imprint","IMPRINT",FACE,{"disambiguationData":[TD([[makeQuery(id+"F0.imprint","IMPRINT",EDGE,{"derivedFrom":sQuery(id+"F0.wireOp",EDGE,"E114.MirrorCS")}),-1.0]])]});
            var Q11;
            Q11=makeQuery(id+"F0.imprint","IMPRINT",FACE,{"disambiguationData":[TD([[makeQuery(id+"F0.imprint","IMPRINT",EDGE,{"derivedFrom":sQuery(id+"F0.wireOp",EDGE,"E192.MirrorC")}),1.0]])]});
            var Q12;
            Q12=makeQuery(id+"F0.imprint","IMPRINT",FACE,{"disambiguationData":[TD([[makeQuery(id+"F0.imprint","IMPRINT",EDGE,{"derivedFrom":sQuery(id+"F0.wireOp",EDGE,"E54.MirrorCS")}),-1.0]])]});
            var Q13;
            Q13=makeQuery(id+"F0.imprint","IMPRINT",FACE,{"disambiguationData":[TD([[makeQuery(id+"F0.imprint","IMPRINT",EDGE,{"derivedFrom":sQuery(id+"F0.wireOp",EDGE,"E53.MirrorCS")}),-1.0]])]});
            var Q14;
            {var subQ8=sQuery(id+"F0.wireOp",EDGE,"E25");Q14=makeQuery(id+"F0.imprint","IMPRINT",FACE,{"disambiguationData":[TD([[makeQuery(id+"F0.imprint","IMPRINT",EDGE,{"derivedFrom":subQ8}),1.0]])]});}
            var Q15;
            Q15=makeQuery(id+"F0.imprint","IMPRINT",FACE,{"disambiguationData":[TD([[makeQuery(id+"F0.imprint","IMPRINT",EDGE,{"derivedFrom":sQuery(id+"F0.wireOp",EDGE,"E58.MirrorCS")}),-1.0]])]});
            var Q16;
            Q16=makeQuery(id+"F0.imprint","IMPRINT",FACE,{"disambiguationData":[TD([[makeQuery(id+"F0.imprint","IMPRINT",EDGE,{"derivedFrom":sQuery(id+"F0.wireOp",EDGE,"E113.MirrorCS")}),1.0]])]});
            var Q17;
            Q17=makeQuery(id+"F0.imprint","IMPRINT",FACE,{"disambiguationData":[TD([[makeQuery(id+"F0.imprint","IMPRINT",EDGE,{"derivedFrom":sQuery(id+"F0.wireOp",EDGE,"E119.MirrorCS")}),-1.0]])]});
            var Q18;
            Q18=makeQuery(id+"F0.imprint","IMPRINT",FACE,{"disambiguationData":[TD([[makeQuery(id+"F0.imprint","IMPRINT",EDGE,{"derivedFrom":sQuery(id+"F0.wireOp",EDGE,"E158.MirrorC")}),-1.0]])]});
            var Q19;
            {var subQ13=sQuery(id+"F0.wireOp",EDGE,"E50");Q19=makeQuery(id+"F0.imprint","IMPRINT",FACE,{"disambiguationData":[TD([[makeQuery(id+"F0.imprint","IMPRINT",EDGE,{"derivedFrom":subQ13}),-1.0]])]});}
            var Q20;
            Q20=makeQuery(id+"F0.imprint","IMPRINT",FACE,{"disambiguationData":[TD([[makeQuery(id+"F0.imprint","IMPRINT",EDGE,{"derivedFrom":sQuery(id+"F0.wireOp",EDGE,"E201.MirrorC")}),1.0]])]});
            extrude(context, id + "F1", {"entities" : qUnion([Q0, Q1, Q2, Q3, Q4, Q5, Q6, Q7, Q8, Q9, Q10, Q11, Q12, Q13, Q14, Q15, Q16, Q17, Q18, Q19, Q20]), "depth" : 750 * mm});
        }
    });
